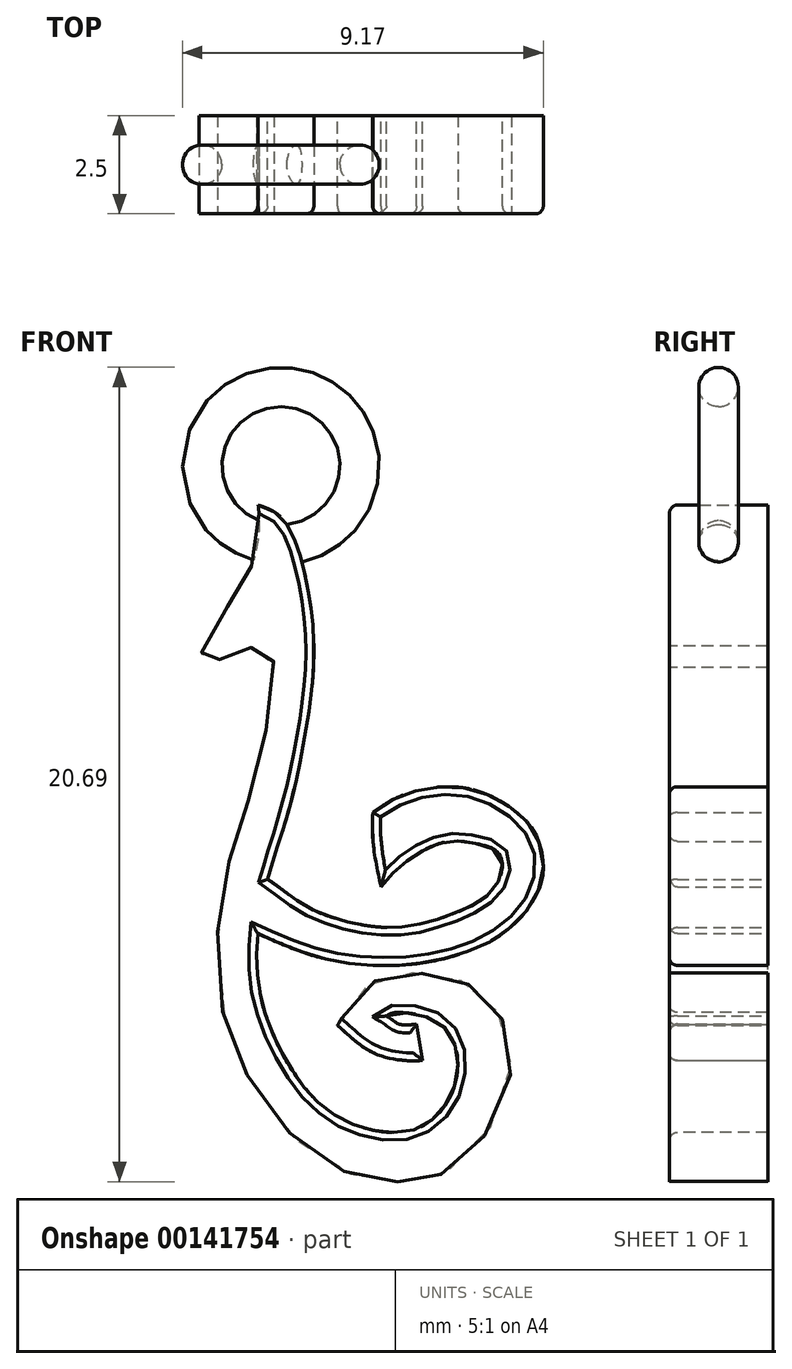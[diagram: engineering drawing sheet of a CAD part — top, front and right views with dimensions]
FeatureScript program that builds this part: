
annotation { "Feature Type Name" : "Feature", "Feature Type Description" : "" }
export const myFeature = defineFeature(function(context is Context, id is Id, definition is map)
    precondition{}
    {
        {
            var Q0;
            Q0=qCreatedBy(makeId("Front.planeOp"),FACE);
            var sketch = newSketch(context, id + "F0", { "sketchPlane" : qUnion([Q0])});
            skLineSegment(sketch, "E0.bottom", {"start": v(-7.5, 0) * mm, "end": v(9.5, 0) * mm, "construction": true});
            skLineSegment(sketch, "E0.top", {"start": v(-7.5, 17) * mm, "end": v(9.5, 17) * mm, "construction": true});
            skLineSegment(sketch, "E0.left", {"start": v(-7.5, 0) * mm, "end": v(-7.5, 17) * mm, "construction": true});
            skLineSegment(sketch, "E0.right", {"start": v(9.5, 0) * mm, "end": v(9.5, 17) * mm, "construction": true});
            skLineSegment(sketch, "E1", {"start": v(0, 0) * mm, "end": v(0, 23.23) * mm, "construction": true});
            skFitSpline(sketch, "E2", {"points": [v(-2.01, 17) * mm, v(-2.1, 15.68) * mm, v(-2.6, 14.7) * mm, v(-3.2, 13.77) * mm, v(-3.49, 12.89) * mm, v(-2.9, 13.13) * mm, v(-2.44, 13.32) * mm, v(-1.94, 13.42) * mm, v(-1.67, 13.22) * mm, v(-1.82, 11.23) * mm, v(-2.44, 8.95) * mm, v(-2.95, 7.1) * mm, v(-2.93, 4.2) * mm, v(-2.08, 2.16) * mm, v(-0.47, 0.4) * mm, v(1.09, -0.16) * mm, v(2.12, -0.14) * mm, v(3.04, 0.23) * mm, v(4.24, 1.9) * mm, v(4.33, 3.53) * mm, v(3.7, 4.58) * mm, v(2.73, 5.03) * mm, v(1.63, 5.1) * mm, v(0.65, 4.71) * mm, v(0, 3.78) * mm], "startDerivative": vector(3.51, -28.57) * mm, "endDerivative": vector(-9.9, -17.08) * mm});
            skFitSpline(sketch, "E3", {"points": [v(0, 3.78) * mm, v(0.96, 3.06) * mm, v(2.16, 2.9) * mm], "startDerivative": vector(1.82, -1.62) * mm, "endDerivative": vector(1.77, 0.22) * mm});
            skLineSegment(sketch, "E4", {"start": v(2.16, 2.9) * mm, "end": v(2.01, 3.81) * mm});
            skFitSpline(sketch, "E5", {"points": [v(2.01, 3.81) * mm, v(1.56, 3.81) * mm, v(1.24, 4.02) * mm], "startDerivative": vector(-0.86, -0.08) * mm, "endDerivative": vector(-0.67, 0.39) * mm});
            skFitSpline(sketch, "E6", {"points": [v(1.24, 4.02) * mm, v(1.63, 4.1) * mm, v(2.61, 3.83) * mm, v(3.05, 2.98) * mm, v(2.87, 1.98) * mm, v(2.32, 1.32) * mm, v(1.63, 1.06) * mm, v(0.23, 1.34) * mm, v(-0.95, 2.35) * mm, v(-1.8, 3.96) * mm, v(-2.06, 5.52) * mm, v(-1.77, 7.5) * mm, v(-1.28, 9.12) * mm, v(-0.75, 11.63) * mm, v(-0.63, 14) * mm, v(-1.11, 16.18) * mm, v(-1.44, 16.7) * mm, v(-2.01, 17) * mm], "startDerivative": vector(9.88, 7.94) * mm, "endDerivative": vector(-24.06, 7.56) * mm});
            skFitSpline(sketch, "E7", {"points": [v(-1.77, 7.5) * mm, v(-0.67, 6.74) * mm, v(1.33, 6.27) * mm, v(2.78, 6.56) * mm, v(3.63, 6.96) * mm, v(4.12, 7.5) * mm, v(4.1, 8.14) * mm, v(3.43, 8.42) * mm, v(2.66, 8.42) * mm, v(1.7, 7.91) * mm, v(1.1, 7.3) * mm], "startDerivative": vector(12.7, -8.61) * mm, "endDerivative": vector(-6.05, -7.17) * mm});
            skFitSpline(sketch, "E8", {"points": [v(1.1, 7.3) * mm, v(0.9, 8.5) * mm, v(0.9, 9.19) * mm], "startDerivative": vector(-0.46, 2.24) * mm, "endDerivative": vector(0.08, 1.5) * mm});
            skFitSpline(sketch, "E9", {"points": [v(-2.02, 6.11) * mm, v(-0.62, 5.55) * mm, v(0.65, 5.33) * mm, v(2.15, 5.37) * mm, v(3.8, 5.87) * mm, v(4.7, 6.59) * mm, v(5.14, 7.3) * mm, v(5.22, 7.9) * mm, v(4.96, 8.76) * mm, v(3.99, 9.56) * mm, v(2.88, 9.84) * mm, v(1.66, 9.64) * mm, v(0.9, 9.19) * mm], "startDerivative": vector(15.2, -6.57) * mm, "endDerivative": vector(-9.55, -6.77) * mm});
            skSolve(sketch);
        }
        {
            var Q0;
            Q0=qSketchRegion(id+"F0",true);
            extrude(context, id + "F1", {"entities" : qUnion([Q0]), "depth" : 2.5 * mm});
        }
        {
            var Q0;
            Q0=qCreatedBy(makeId("Right.planeOp"),FACE);
            cPlane(context, id + "F2", {"entities" : qUnion([Q0]), "cplaneType" : CPlaneType.OFFSET, "offset" : 1.44 * mm, "oppositeDirection" : true, "width" : 150 * mm, "height" : 150 * mm});
        }
        {
            var Q0;
            Q0=qCreatedBy(id+"F2.planeOp",FACE);
            var sketch = newSketch(context, id + "F3", { "sketchPlane" : qUnion([Q0])});
            skCircle(sketch, "E10", {"center": v(-1.25, 16) * mm, "radius": 0.5 * mm});
            skLineSegment(sketch, "E11", {"start": v(-3.17, 18) * mm, "end": v(2.9, 18) * mm, "construction": true});
            skSolve(sketch);
        }
        {
            var Q0;
            Q0=qSketchRegion(id+"F3",true);
            var Q1;
            Q1=sQuery(id+"F3.wireOp",EDGE,"E11");
            revolve(context, id + "F4", {"operationType" : NewBodyOperationType.ADD, "entities" : qUnion([Q0]), "axis" : qUnion([Q1]), "revolveType" : RevolveType.FULL});
        }
        {
            var Q0;
            {var subQ0=sQuery(id+"F0.wireOp",EDGE,"E6");Q0=makeQuery(id+"F1.opExtrude","CAP_EDGE",EDGE,{"disambiguationData":[OSD([subQ0]),TDD([makeQuery(id+"F0.imprint","IMPRINT",EDGE,{"disambiguationData":[TD([[makeQuery(id+"F0.imprint","INTERSECT",VERTEX,{"derivedFrom":[sQuery(id+"F0.wireOp",EDGE,"E5"),subQ0]}),-1.0]])],"derivedFrom":subQ0})])],"isStart":false});}
            var Q1;
            Q1=makeQuery(id+"F1.opExtrude","CAP_EDGE",EDGE,{"disambiguationData":[OSD([sQuery(id+"F0.wireOp",EDGE,"E5")])],"isStart":false});
            var Q2;
            Q2=makeQuery(id+"F1.opExtrude","CAP_EDGE",EDGE,{"disambiguationData":[OSD([sQuery(id+"F0.wireOp",EDGE,"E4")])],"isStart":false});
            var Q3;
            Q3=makeQuery(id+"F1.opExtrude","CAP_EDGE",EDGE,{"disambiguationData":[OSD([sQuery(id+"F0.wireOp",EDGE,"E3")])],"isStart":false});
            var Q4;
            Q4=makeQuery(id+"F1.opExtrude","CAP_EDGE",EDGE,{"disambiguationData":[OSD([sQuery(id+"F0.wireOp",EDGE,"E9")])],"isStart":false});
            var Q5;
            Q5=makeQuery(id+"F1.opExtrude","CAP_EDGE",EDGE,{"disambiguationData":[OSD([sQuery(id+"F0.wireOp",EDGE,"E8")])],"isStart":false});
            var Q6;
            Q6=makeQuery(id+"F1.opExtrude","CAP_EDGE",EDGE,{"disambiguationData":[OSD([sQuery(id+"F0.wireOp",EDGE,"E7")])],"isStart":false});
            var Q7;
            {var subQ0=sQuery(id+"F0.wireOp",EDGE,"E6");Q7=makeQuery(id+"F1.opExtrude","CAP_EDGE",EDGE,{"disambiguationData":[OSD([subQ0]),TDD([makeQuery(id+"F0.imprint","IMPRINT",EDGE,{"disambiguationData":[TD([[makeQuery(id+"F0.imprint","INTERSECT",VERTEX,{"derivedFrom":[sQuery(id+"F0.wireOp",EDGE,"E2"),subQ0]}),1.0]])],"derivedFrom":subQ0})])],"isStart":false});}
            fillet(context, id + "F5", {"entities" : qUnion([Q0, Q1, Q2, Q3, Q4, Q5, Q6, Q7]), "radius" : 0.2 * mm, "tangentPropagation" : true, "allowEdgeOverflow" : false});
        }
    });
